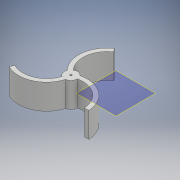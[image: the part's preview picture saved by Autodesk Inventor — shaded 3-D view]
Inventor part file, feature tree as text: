
AUTODESK INVENTOR PART (.ipt)
format: ipt  version: 2017 (Build 210142000, 142)  size: 130,048 bytes
history: native  units: mm
features: sketch x2, plane x1, extrude x1, hole x1
ambient origin geometry x8: Origin, YZ Plane, XZ Plane, XY Plane, X Axis, Y Axis, Z Axis, Center Point
bodies: Body1 (feature_tree)
feature tree (5):
  plane  "Work Plane4"
  extrude  "Extrusion2"  Depth=13.200081mm
  hole  "Hole1"  [1 undecoded]
  sketch  "Sketch5"  dims[d11=3.599914mm d13=13.200081mm]
  sketch  "Sketch6"  dims[d14=15.600167mm d15=13.200001mm d16=15.599945mm d17=13.200103mm d18=15.600096mm d19=14.0mm d20=0.0mm d21=3.0mm d22=1.0mm d23=6.0mm d24=4.0mm d25=2.0mm d26=90.0deg d27=14.0mm d28=20.594885mm]
note: 1 required parameter value undecoded (feature->parameter linkage not recoverable at this tier; creation-order binding heuristic only, values carry confidence <= 0.55)
